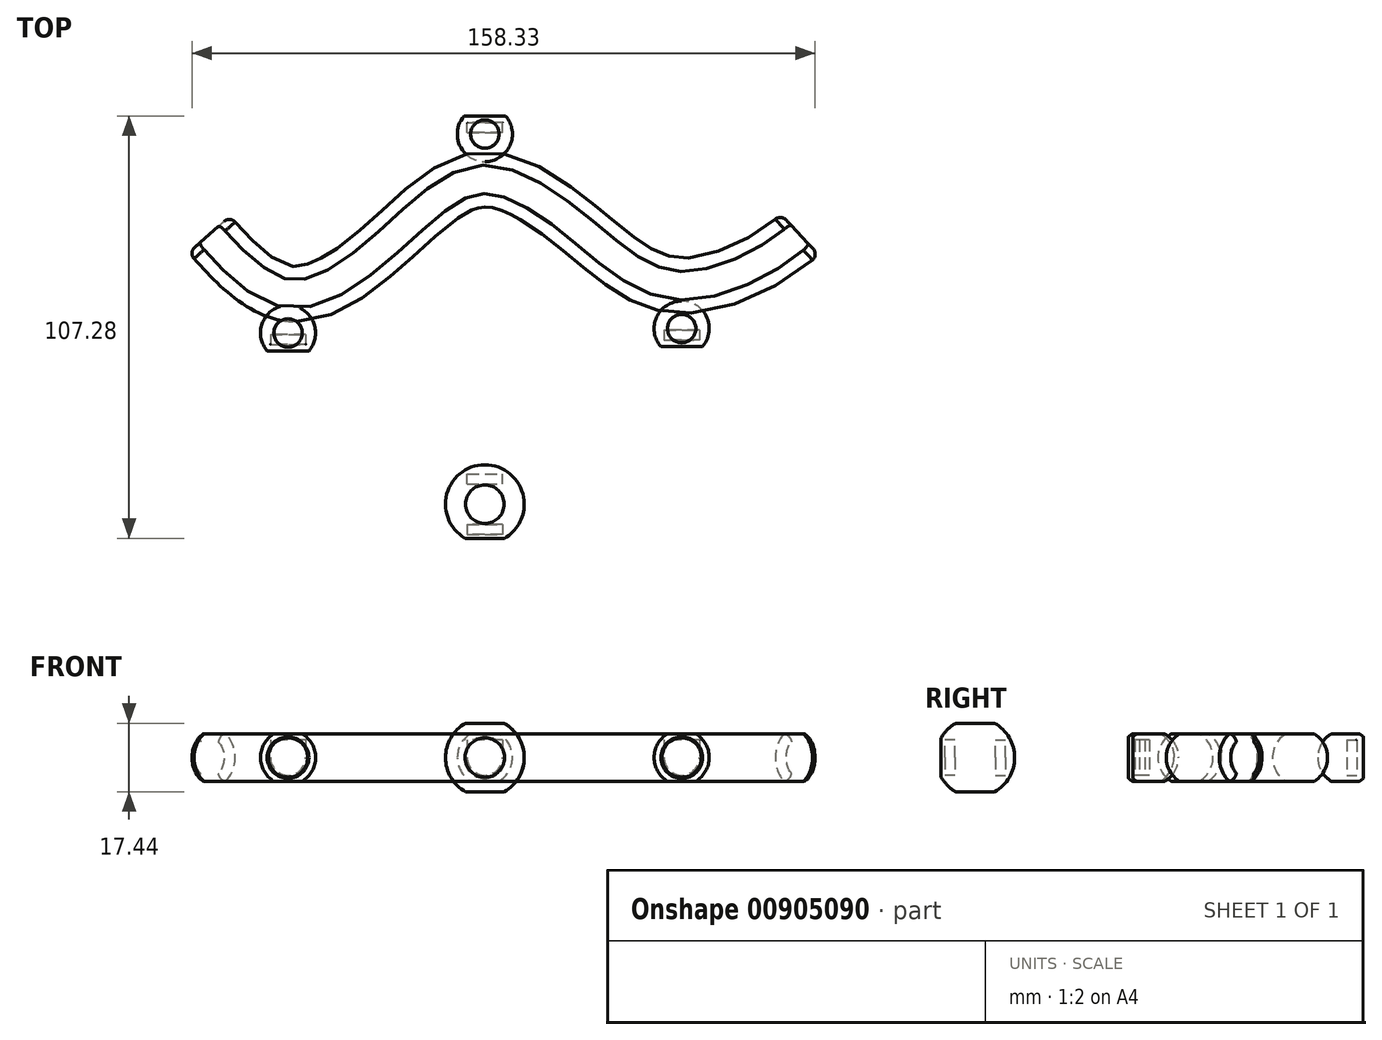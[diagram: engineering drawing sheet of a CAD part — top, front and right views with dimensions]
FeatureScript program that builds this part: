
annotation { "Feature Type Name" : "Feature", "Feature Type Description" : "" }
export const myFeature = defineFeature(function(context is Context, id is Id, definition is map)
    precondition{}
    {
        {
            var Q0;
            Q0=qCreatedBy(makeId("Top.planeOp"),FACE);
            var sketch = newSketch(context, id + "F0", { "sketchPlane" : qUnion([Q0])});
            skFitSpline(sketch, "E0", {"points": [v(-30.73, 0) * mm, v(-10.73, -15) * mm, v(16.81, 0) * mm, v(39.27, 14) * mm, v(65.21, 0) * mm, v(89.27, -13) * mm, v(119.27, 0) * mm], "startDerivative": vector(86.91, -95.71) * mm, "endDerivative": vector(111.5, 106.41) * mm});
            skSolve(sketch);
        }
        {
            var Q0;
            Q0=qCreatedBy(makeId("Right.planeOp"),FACE);
            var Q1;
            Q1=sQuery(id+"F0.wireOp",VERTEX,"E0.3.internal");
            cPlane(context, id + "F1", {"entities" : qUnion([Q0, Q1]), "cplaneType" : CPlaneType.PLANE_POINT, "offset" : 25 * mm, "width" : 150 * mm, "height" : 150 * mm});
        }
        {
            var Q0;
            Q0=qCreatedBy(id+"F1.planeOp",FACE);
            var sketch = newSketch(context, id + "F2", { "sketchPlane" : qUnion([Q0])});
            skPoint(sketch, "E1.0", {"position": v(14, 0) * mm});
            skArc(sketch, "E2", {"start": v(10.4, 6) * mm, "mid": v(7, 0) * mm, "end": v(10.4, -6) * mm});
            skLineSegment(sketch, "E3", {"start": v(17.6, -6) * mm, "end": v(17.6, -6) * mm});
            skLineSegment(sketch, "E4", {"start": v(17.6, 6) * mm, "end": v(10.4, 6) * mm});
            skArc(sketch, "E5.trimOffspring", {"start": v(17.6, -6) * mm, "mid": v(21, 0) * mm, "end": v(17.6, 6) * mm});
            skLineSegment(sketch, "E6", {"start": v(17.6, -6) * mm, "end": v(10.4, -6) * mm});
            skSolve(sketch);
        }
        {
            var Q0;
            Q0=makeQuery(id+"F2.imprint","IMPRINT",FACE,{"disambiguationData":[TD([[makeQuery(id+"F2.imprint","IMPRINT",EDGE,{"derivedFrom":sQuery(id+"F2.wireOp",EDGE,"E2")}),1.0]])]});
            var Q1;
            Q1=sQuery(id+"F0.wireOp",EDGE,"E0");
            sweep(context, id + "F3", {"profiles" : qUnion([Q0]), "path" : qUnion([Q1])});
        }
        {
            var Q0;
            Q0=qCreatedBy(id+"F1.planeOp",FACE);
            var sketch = newSketch(context, id + "F4", { "sketchPlane" : qUnion([Q0])});
            skArc(sketch, "E7", {"start": v(30.1, 5.28) * mm, "mid": v(30.01, 5.14) * mm, "end": v(29.93, 5) * mm});
            skLineSegment(sketch, "E8", {"start": v(18.5, 0) * mm, "end": v(29.93, 0) * mm});
            skPoint(sketch, "E9.0", {"position": v(17.32, -6) * mm});
            skPoint(sketch, "E10.0", {"position": v(17.32, 6) * mm});
            skArc(sketch, "E11.trimOffspring", {"start": v(30.1, 5.28) * mm, "mid": v(18.5, 0) * mm, "end": v(30.1, -5.28) * mm});
            skLineSegment(sketch, "E12", {"start": v(29.93, 5) * mm, "end": v(29.93, -5) * mm});
            skArc(sketch, "E13.trimOffspring", {"start": v(29.93, -5) * mm, "mid": v(30.01, -5.14) * mm, "end": v(30.1, -5.28) * mm});
            skPoint(sketch, "E14.orphan", {"position": v(28.59, 0) * mm});
            skPoint(sketch, "E15", {"position": v(28.43, 0) * mm});
            skSolve(sketch);
        }
        {
            var Q0;
            {var subQ3=sQuery(id+"F4.wireOp",EDGE,"E8");Q0=makeQuery(id+"F4.imprint","IMPRINT",FACE,{"disambiguationData":[TD([[makeQuery(id+"F4.imprint","IMPRINT",EDGE,{"derivedFrom":subQ3}),1.0]])]});}
            var Q1;
            Q1=sQuery(id+"F4.wireOp",EDGE,"E8");
            revolve(context, id + "F5", {"surfaceOperationType" : NewSurfaceOperationType.NEW, "entities" : qUnion([Q0]), "axis" : qUnion([Q1]), "revolveType" : RevolveType.FULL});
        }
        {
            var Q0;
            Q0=qCreatedBy(makeId("Front.planeOp"),FACE);
            var Q1;
            Q1=sQuery(id+"F4.wireOp",VERTEX,"E15");
            cPlane(context, id + "F6", {"entities" : qUnion([Q0, Q1]), "cplaneType" : CPlaneType.PLANE_POINT, "offset" : 25 * mm, "width" : 150 * mm, "height" : 150 * mm});
        }
        {
            var Q0;
            Q0=qCreatedBy(id+"F6.planeOp",FACE);
            var sketch = newSketch(context, id + "F7", { "sketchPlane" : qUnion([Q0])});
            skPoint(sketch, "E16.0", {"position": v(39.27, 0) * mm});
            skArc(sketch, "E17", {"start": v(34.77, 0) * mm, "mid": v(39.27, -4.5) * mm, "end": v(43.77, 0) * mm});
            skLineSegment(sketch, "E18", {"start": v(39.27, 4.5) * mm, "end": v(34.77, 4.5) * mm});
            skLineSegment(sketch, "E19", {"start": v(34.77, 4.5) * mm, "end": v(34.77, 0) * mm});
            skLineSegment(sketch, "E20.MirrorCS", {"start": v(39.27, 4.5) * mm, "end": v(43.77, 4.5) * mm});
            skLineSegment(sketch, "E21.MirrorCS", {"start": v(43.77, 4.5) * mm, "end": v(43.77, 0) * mm});
            skPoint(sketch, "E22.orphan", {"position": v(39.27, 5.28) * mm});
            skPoint(sketch, "E23.0.end.orphan", {"position": v(39.27, 5) * mm});
            skSolve(sketch);
        }
        {
            var Q0;
            Q0=makeQuery(id+"F7.imprint","IMPRINT",FACE,{"disambiguationData":[TD([[makeQuery(id+"F7.imprint","IMPRINT",EDGE,{"derivedFrom":sQuery(id+"F7.wireOp",EDGE,"E17")}),1.0]])]});
            extrude(context, id + "F8", {"entities" : qUnion([Q0]), "operationType" : NewBodyOperationType.REMOVE, "depth" : 2.5 * mm, "offsetDistance" : 25 * mm});
        }
        {
            var Q0;
            Q0=qCreatedBy(makeId("Top.planeOp"),FACE);
            var Q1;
            Q1=sQuery(id+"F4.wireOp",VERTEX,"E10.0");
            cPlane(context, id + "F9", {"entities" : qUnion([Q0, Q1]), "cplaneType" : CPlaneType.PLANE_POINT, "offset" : 25 * mm, "width" : 150 * mm, "height" : 150 * mm});
        }
        {
            var Q0;
            Q0=qCreatedBy(id+"F9.planeOp",FACE);
            var sketch = newSketch(context, id + "F10", { "sketchPlane" : qUnion([Q0])});
            skArc(sketch, "E24", {"start": v(34, 30.1) * mm, "mid": v(39.27, 18.5) * mm, "end": v(44.56, 30.1) * mm});
            skLineSegment(sketch, "E25.0", {"start": v(44.56, 30.1) * mm, "end": v(34, 30.1) * mm});
            skSolve(sketch);
        }
        {
            var Q0;
            Q0=makeQuery(id+"F10.imprint","IMPRINT",FACE,{"disambiguationData":[TD([[makeQuery(id+"F10.imprint","IMPRINT",EDGE,{"derivedFrom":sQuery(id+"F10.wireOp",EDGE,"E24")}),1.0]])]});
            extrude(context, id + "F11", {"entities" : qUnion([Q0]), "operationType" : NewBodyOperationType.REMOVE, "endBound" : BoundingType.THROUGH_ALL, "depth" : 25 * mm, "offsetDistance" : 25 * mm});
        }
        {
            var Q0;
            Q0=makeQuery(id+"F3.opSweep","SWEPT_EDGE",EDGE,{"disambiguationData":[OSD([sQuery(id+"F0.wireOp",EDGE,"E0"),sQuery(id+"F2.wireOp",EDGE,"E5.trimOffspring"),sQuery(id+"F2.wireOp",EDGE,"E6")])]});
            cPoint(context, id + "F12", {"entities" : qUnion([Q0]), "parameter" : 0.5});
        }
        {
            var Q0;
            Q0=qCreatedBy(makeId("Top.planeOp"),FACE);
            var Q1;
            Q1 = qCreatedBy(id + "F12" ,VERTEX);
            cPlane(context, id + "F13", {"entities" : qUnion([Q0, Q1]), "cplaneType" : CPlaneType.PLANE_POINT, "offset" : 25 * mm, "width" : 150 * mm, "height" : 150 * mm});
        }
        {
            var Q0;
            Q0=qCreatedBy(id+"F13.planeOp",FACE);
            var sketch = newSketch(context, id + "F14", { "sketchPlane" : qUnion([Q0])});
            skArc(sketch, "E26", {"start": v(34, 30.1) * mm, "mid": v(39.27, 18.5) * mm, "end": v(44.56, 30.1) * mm});
            skLineSegment(sketch, "E27.0", {"start": v(44.56, 30.1) * mm, "end": v(34, 30.1) * mm});
            skSolve(sketch);
        }
        {
            var Q0;
            Q0=makeQuery(id+"F14.imprint","IMPRINT",FACE,{"disambiguationData":[TD([[makeQuery(id+"F14.imprint","IMPRINT",EDGE,{"derivedFrom":sQuery(id+"F14.wireOp",EDGE,"E26")}),1.0]])]});
            extrude(context, id + "F15", {"entities" : qUnion([Q0]), "operationType" : NewBodyOperationType.REMOVE, "endBound" : BoundingType.THROUGH_ALL, "oppositeDirection" : true, "depth" : 25 * mm, "offsetDistance" : 25 * mm});
        }
        {
            var Q0;
            Q0=makeQuery(id+"F5.opRevolve","SWEPT_BODY",BODY,{"disambiguationData":[OSD([sQuery(id+"F4.wireOp",EDGE,"E7"),sQuery(id+"F4.wireOp",EDGE,"E8"),sQuery(id+"F4.wireOp",EDGE,"E11.trimOffspring")])]});
            var Q1;
            Q1=qCreatedBy(makeId("Front.planeOp"),FACE);
            mirror(context, id + "F16", {"entities" : qUnion([Q0]), "mirrorPlane" : qUnion([Q1])});
        }
        {
            var Q0;
            Q0=makeQuery(id+"F16.opPattern","COPY",BODY,{"derivedFrom":makeQuery(id+"F5.opRevolve","SWEPT_BODY",BODY,{"disambiguationData":[OSD([sQuery(id+"F4.wireOp",EDGE,"E7"),sQuery(id+"F4.wireOp",EDGE,"E8"),sQuery(id+"F4.wireOp",EDGE,"E11.trimOffspring")])]}),"instanceName":"1"});
            transform(context, id + "F17", {"entities" : qUnion([Q0]), "transformType" : TransformType.TRANSLATION_3D, "dx" : 50 * mm, "dy" : 1.6 * mm, "dz" : 0 * mm, "makeCopy" : false});
        }
        {
            var Q0;
            Q0=makeQuery(id+"F16.opPattern","COPY",BODY,{"derivedFrom":makeQuery(id+"F5.opRevolve","SWEPT_BODY",BODY,{"disambiguationData":[OSD([sQuery(id+"F4.wireOp",EDGE,"E7"),sQuery(id+"F4.wireOp",EDGE,"E8"),sQuery(id+"F4.wireOp",EDGE,"E11.trimOffspring")])]}),"instanceName":"1"});
            transform(context, id + "F18", {"entities" : qUnion([Q0]), "transformType" : TransformType.TRANSLATION_3D, "dx" : -100 * mm, "dy" : -1.1 * mm, "dz" : 0 * mm, "makeCopy" : true});
        }
        {
            var Q0;
            Q0=makeQuery(id+"F18.opPattern","COPY",BODY,{"derivedFrom":makeQuery(id+"F16.opPattern","COPY",BODY,{"derivedFrom":makeQuery(id+"F5.opRevolve","SWEPT_BODY",BODY,{"disambiguationData":[OSD([sQuery(id+"F4.wireOp",EDGE,"E7"),sQuery(id+"F4.wireOp",EDGE,"E8"),sQuery(id+"F4.wireOp",EDGE,"E11.trimOffspring")])]}),"instanceName":"1"}),"instanceName":"1"});
            transform(context, id + "F19", {"entities" : qUnion([Q0]), "transformType" : TransformType.TRANSLATION_3D, "dx" : 0 * mm, "dy" : -32.9 * mm, "dz" : 0 * mm, "makeCopy" : true});
        }
        {
            var Q0;
            Q0=makeQuery(id+"F3.opSweep","CAP_FACE",FACE,{"disambiguationData":[OSD([sQuery(id+"F0.wireOp",VERTEX,"E0.end"),sQuery(id+"F2.wireOp",EDGE,"E2"),sQuery(id+"F2.wireOp",EDGE,"E4"),sQuery(id+"F2.wireOp",EDGE,"E5.trimOffspring"),sQuery(id+"F2.wireOp",EDGE,"E6")])],"isStart":false});
            var Q1;
            Q1=makeQuery(id+"F3.opSweep","CAP_FACE",FACE,{"disambiguationData":[OSD([sQuery(id+"F0.wireOp",VERTEX,"E0.start"),sQuery(id+"F2.wireOp",EDGE,"E2"),sQuery(id+"F2.wireOp",EDGE,"E4"),sQuery(id+"F2.wireOp",EDGE,"E5.trimOffspring"),sQuery(id+"F2.wireOp",EDGE,"E6")])],"isStart":true});
            fillet(context, id + "F20", {"entities" : qUnion([Q0, Q1]), "radius" : 2 * mm, "tangentPropagation" : true, "allowEdgeOverflow" : false});
        }
        {
            var Q0;
            Q0=makeQuery(id+"F19.opPattern","COPY",BODY,{"derivedFrom":makeQuery(id+"F18.opPattern","COPY",BODY,{"derivedFrom":makeQuery(id+"F16.opPattern","COPY",BODY,{"derivedFrom":makeQuery(id+"F5.opRevolve","SWEPT_BODY",BODY,{"disambiguationData":[OSD([sQuery(id+"F4.wireOp",EDGE,"E7"),sQuery(id+"F4.wireOp",EDGE,"E8"),sQuery(id+"F4.wireOp",EDGE,"E11.trimOffspring")])]}),"instanceName":"1"}),"instanceName":"1"}),"instanceName":"1"});
            deleteBodies(context, id + "F21", {"entities" : qUnion([Q0])});
        }
        {
            var Q0;
            Q0=qCreatedBy(id+"F1.planeOp",FACE);
            var sketch = newSketch(context, id + "F22", { "sketchPlane" : qUnion([Q0])});
            skArc(sketch, "E28", {"start": v(-73.42, 8.72) * mm, "mid": v(-77.15, 5.05) * mm, "end": v(-78.52, 0) * mm});
            skLineSegment(sketch, "E29", {"start": v(-73.42, 8.72) * mm, "end": v(-63.62, 8.72) * mm});
            skLineSegment(sketch, "E30", {"start": v(-78.52, 0) * mm, "end": v(-58.52, 0) * mm});
            skArc(sketch, "E31.trimOffspring", {"start": v(-58.52, 0) * mm, "mid": v(-59.9, 5.05) * mm, "end": v(-63.62, 8.72) * mm});
            skArc(sketch, "E32.MirrorCS", {"start": v(-73.42, -8.72) * mm, "mid": v(-77.15, -5.05) * mm, "end": v(-78.52, 0) * mm});
            skLineSegment(sketch, "E33.MirrorCS", {"start": v(-73.42, -8.72) * mm, "end": v(-63.62, -8.72) * mm});
            skArc(sketch, "E34.MirrorCS", {"start": v(-58.52, 0) * mm, "mid": v(-59.9, -5.05) * mm, "end": v(-63.62, -8.72) * mm});
            skLineSegment(sketch, "E35", {"start": v(-68.52, 8.72) * mm, "end": v(-68.52, -8.72) * mm});
            skLineSegment(sketch, "E36", {"start": v(-63.62, 8.72) * mm, "end": v(-63.62, -8.72) * mm});
            skLineSegment(sketch, "E37", {"start": v(-73.42, -8.72) * mm, "end": v(-73.42, 8.72) * mm});
            skLineSegment(sketch, "E38", {"start": v(-77.18, 5) * mm, "end": v(-77.18, -5) * mm});
            skLineSegment(sketch, "E39", {"start": v(-59.86, 5) * mm, "end": v(-59.86, -5) * mm});
            skPoint(sketch, "E40", {"position": v(-76.18, 0) * mm});
            skPoint(sketch, "E41", {"position": v(-60.86, 0) * mm});
            skSolve(sketch);
        }
        {
            var Q0;
            {var subQ0=sQuery(id+"F22.wireOp",EDGE,"E31.trimOffspring");var subQ3=sQuery(id+"F22.wireOp",EDGE,"E39");var subQ5=makeQuery(id+"F22.imprint","INTERSECT",VERTEX,{"derivedFrom":[subQ0,subQ3]});Q0=makeQuery(id+"F22.imprint","IMPRINT",FACE,{"disambiguationData":[TD([[makeQuery(id+"F22.imprint","IMPRINT",EDGE,{"disambiguationData":[TD([[subQ5,-1.0]])],"derivedFrom":subQ3}),1.0]])]});}
            var Q1;
            {var subQ0=sQuery(id+"F22.wireOp",EDGE,"E34.MirrorCS");var subQ3=sQuery(id+"F22.wireOp",EDGE,"E39");var subQ5=makeQuery(id+"F22.imprint","INTERSECT",VERTEX,{"derivedFrom":[subQ0,subQ3]});Q1=makeQuery(id+"F22.imprint","IMPRINT",FACE,{"disambiguationData":[TD([[makeQuery(id+"F22.imprint","IMPRINT",EDGE,{"disambiguationData":[TD([[subQ5,1.0]])],"derivedFrom":subQ3}),1.0]])]});}
            var Q2;
            {var subQ0=sQuery(id+"F22.wireOp",EDGE,"E36");var subQ1=sQuery(id+"F22.wireOp",EDGE,"E30");var subQ2=makeQuery(id+"F22.imprint","INTERSECT",VERTEX,{"derivedFrom":[subQ1,subQ0]});Q2=makeQuery(id+"F22.imprint","IMPRINT",FACE,{"disambiguationData":[TD([[makeQuery(id+"F22.imprint","IMPRINT",EDGE,{"disambiguationData":[TD([[subQ2,-1.0]])],"derivedFrom":subQ1}),-1.0]])]});}
            var Q3;
            {var subQ0=sQuery(id+"F22.wireOp",EDGE,"E36");var subQ1=sQuery(id+"F22.wireOp",EDGE,"E30");var subQ2=makeQuery(id+"F22.imprint","INTERSECT",VERTEX,{"derivedFrom":[subQ1,subQ0]});Q3=makeQuery(id+"F22.imprint","IMPRINT",FACE,{"disambiguationData":[TD([[makeQuery(id+"F22.imprint","IMPRINT",EDGE,{"disambiguationData":[TD([[subQ2,-1.0]])],"derivedFrom":subQ1}),1.0]])]});}
            var Q4;
            {var subQ3=sQuery(id+"F22.wireOp",EDGE,"E35");var subQ5=sQuery(id+"F22.wireOp",EDGE,"E30");var subQ6=makeQuery(id+"F22.imprint","INTERSECT",VERTEX,{"derivedFrom":[subQ5,subQ3]});Q4=makeQuery(id+"F22.imprint","IMPRINT",FACE,{"disambiguationData":[TD([[makeQuery(id+"F22.imprint","IMPRINT",EDGE,{"disambiguationData":[TD([[subQ6,-1.0]])],"derivedFrom":subQ5}),1.0]])]});}
            var Q5;
            {var subQ0=sQuery(id+"F22.wireOp",EDGE,"E35");var subQ1=sQuery(id+"F22.wireOp",EDGE,"E30");var subQ2=makeQuery(id+"F22.imprint","INTERSECT",VERTEX,{"derivedFrom":[subQ1,subQ0]});Q5=makeQuery(id+"F22.imprint","IMPRINT",FACE,{"disambiguationData":[TD([[makeQuery(id+"F22.imprint","IMPRINT",EDGE,{"disambiguationData":[TD([[subQ2,-1.0]])],"derivedFrom":subQ1}),-1.0]])]});}
            var Q6;
            Q6=sQuery(id+"F22.wireOp",EDGE,"E35");
            revolve(context, id + "F23", {"surfaceOperationType" : NewSurfaceOperationType.NEW, "entities" : qUnion([Q0, Q1, Q2, Q3, Q4, Q5]), "axis" : qUnion([Q6]), "revolveType" : RevolveType.FULL});
        }
        {
            var Q0;
            Q0=qCreatedBy(makeId("Front.planeOp"),FACE);
            var Q1;
            Q1=sQuery(id+"F22.wireOp",VERTEX,"E40");
            cPlane(context, id + "F24", {"entities" : qUnion([Q0, Q1]), "cplaneType" : CPlaneType.PLANE_POINT, "offset" : 25 * mm, "width" : 150 * mm, "height" : 150 * mm});
        }
        {
            var Q0;
            Q0=qCreatedBy(id+"F24.planeOp",FACE);
            var sketch = newSketch(context, id + "F25", { "sketchPlane" : qUnion([Q0])});
            skLineSegment(sketch, "E42.0", {"start": v(43.77, 4.5) * mm, "end": v(34.77, 4.5) * mm});
            skLineSegment(sketch, "E43.0", {"start": v(34.77, 0) * mm, "end": v(34.77, 4.5) * mm});
            skLineSegment(sketch, "E44.0", {"start": v(43.77, 0) * mm, "end": v(43.77, 4.5) * mm});
            skArc(sketch, "E45.0", {"start": v(34.77, 0) * mm, "mid": v(39.27, -4.5) * mm, "end": v(43.77, 0) * mm});
            skSolve(sketch);
        }
        {
            var Q0;
            Q0 = qSketchRegion(id + "F25", true);
            extrude(context, id + "F26", {"entities" : qUnion([Q0]), "operationType" : NewBodyOperationType.REMOVE, "oppositeDirection" : true, "depth" : 2.5 * mm, "offsetDistance" : 25 * mm});
        }
        {
            var Q0;
            Q0=qCreatedBy(id+"F24.planeOp",FACE);
            var Q1;
            Q1=sQuery(id+"F22.wireOp",VERTEX,"E41");
            cPlane(context, id + "F27", {"entities" : qUnion([Q0, Q1]), "cplaneType" : CPlaneType.PLANE_POINT, "offset" : 25 * mm, "width" : 150 * mm, "height" : 150 * mm});
        }
        {
            var Q0;
            Q0=qCreatedBy(id+"F27.planeOp",FACE);
            var sketch = newSketch(context, id + "F28", { "sketchPlane" : qUnion([Q0])});
            skLineSegment(sketch, "E46.0", {"start": v(43.77, 4.5) * mm, "end": v(43.77, 4.5) * mm});
            skLineSegment(sketch, "E47.0", {"start": v(34.77, 4.5) * mm, "end": v(43.77, 4.5) * mm});
            skLineSegment(sketch, "E48.0", {"start": v(34.77, 4.5) * mm, "end": v(34.77, 4.5) * mm});
            skArc(sketch, "E49.0", {"start": v(34.77, 0) * mm, "mid": v(39.27, -4.5) * mm, "end": v(43.77, 0) * mm});
            skLineSegment(sketch, "E50.0", {"start": v(34.77, 0) * mm, "end": v(34.77, 4.5) * mm});
            skLineSegment(sketch, "E51.0", {"start": v(43.77, 0) * mm, "end": v(43.77, 4.5) * mm});
            skSolve(sketch);
        }
        {
            var Q0;
            Q0 = qSketchRegion(id + "F28", true);
            extrude(context, id + "F29", {"entities" : qUnion([Q0]), "operationType" : NewBodyOperationType.REMOVE, "depth" : 2.5 * mm, "offsetDistance" : 25 * mm});
        }
        {
            var Q0;
            Q0=qCreatedBy(id+"F1.planeOp",FACE);
            var sketch = newSketch(context, id + "F30", { "sketchPlane" : qUnion([Q0])});
            skArc(sketch, "E52", {"start": v(-73.42, 8.72) * mm, "mid": v(-68.52, -10) * mm, "end": v(-63.62, 8.72) * mm});
            skLineSegment(sketch, "E53", {"start": v(-77.18, 5) * mm, "end": v(-77.18, -5) * mm});
            skLineSegment(sketch, "E54", {"start": v(-59.86, 5) * mm, "end": v(-59.86, -5) * mm});
            skLineSegment(sketch, "E55", {"start": v(-78.52, 0) * mm, "end": v(-58.52, 0) * mm});
            skPoint(sketch, "E56.orphan", {"position": v(-59.86, 0) * mm});
            skSolve(sketch);
        }
        {
            var Q0;
            {var subQ0=sQuery(id+"F30.wireOp",EDGE,"E53");var subQ1=sQuery(id+"F30.wireOp",EDGE,"E52");var subQ2=makeQuery(id+"F30.imprint","INTERSECT",VERTEX,{"disambiguationData":[OD(1.0)],"derivedFrom":[subQ1,subQ0]});Q0=makeQuery(id+"F30.imprint","IMPRINT",FACE,{"disambiguationData":[TD([[makeQuery(id+"F30.imprint","IMPRINT",EDGE,{"disambiguationData":[TD([[subQ2,1.0]])],"derivedFrom":subQ1}),1.0]])]});}
            var Q1;
            {var subQ0=sQuery(id+"F30.wireOp",EDGE,"E54");var subQ1=sQuery(id+"F30.wireOp",EDGE,"E52");var subQ2=makeQuery(id+"F30.imprint","INTERSECT",VERTEX,{"disambiguationData":[OD(1.0)],"derivedFrom":[subQ1,subQ0]});Q1=makeQuery(id+"F30.imprint","IMPRINT",FACE,{"disambiguationData":[TD([[makeQuery(id+"F30.imprint","IMPRINT",EDGE,{"disambiguationData":[TD([[subQ2,-1.0]])],"derivedFrom":subQ1}),1.0]])]});}
            var Q2;
            Q2=sQuery(id+"F30.wireOp",EDGE,"E55");
            revolve(context, id + "F31", {"operationType" : NewBodyOperationType.REMOVE, "surfaceOperationType" : NewSurfaceOperationType.NEW, "entities" : qUnion([Q0, Q1]), "axis" : qUnion([Q2]), "revolveType" : RevolveType.FULL, "oppositeDirection" : true});
        }
    });
